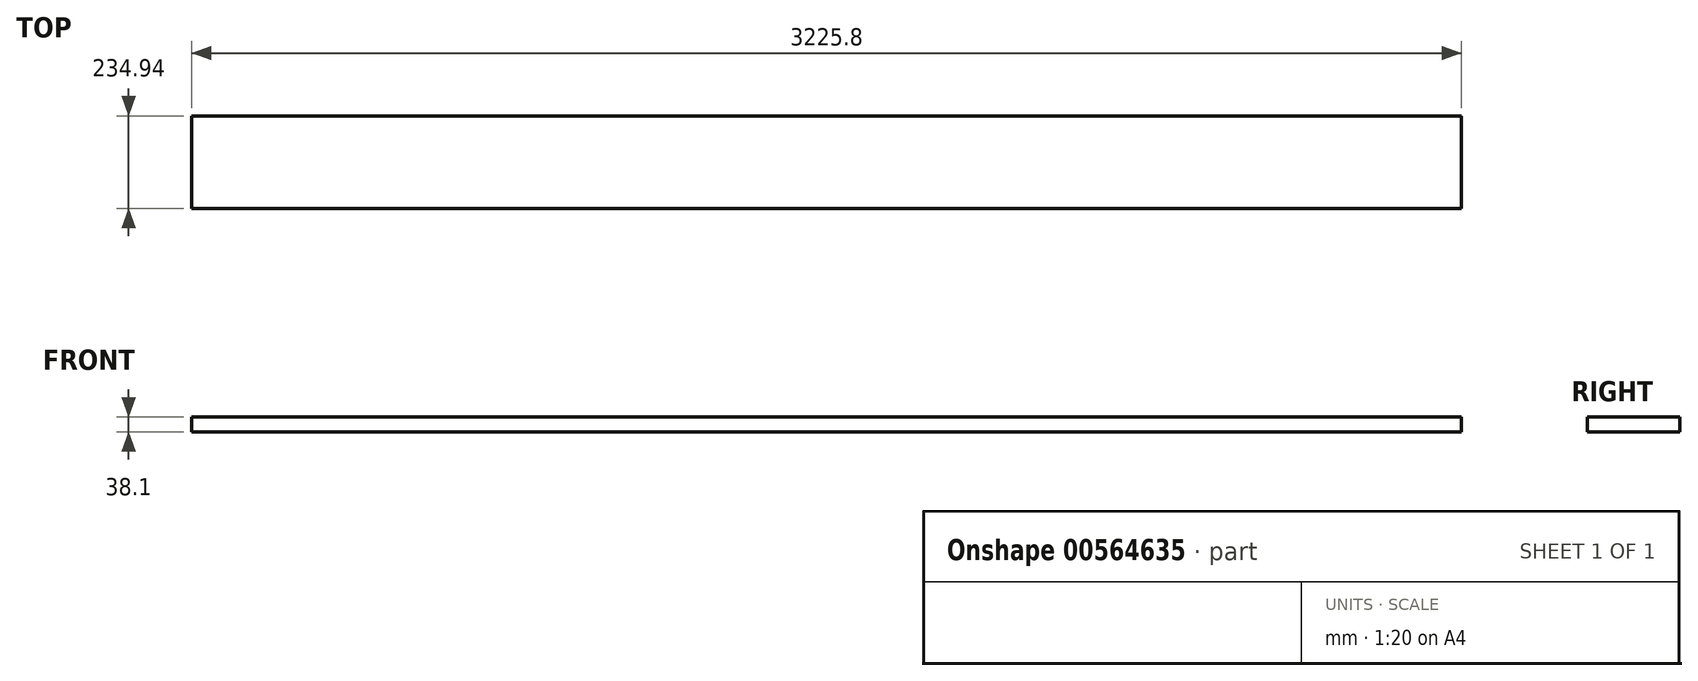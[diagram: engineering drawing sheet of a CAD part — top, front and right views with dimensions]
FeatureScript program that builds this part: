
annotation { "Feature Type Name" : "Feature", "Feature Type Description" : "" }
export const myFeature = defineFeature(function(context is Context, id is Id, definition is map)
    precondition{}
    {
        {
            var Q0;
            Q0=qCreatedBy(makeId("Top.planeOp"),FACE);
            var sketch = newSketch(context, id + "F0", { "sketchPlane" : qUnion([Q0])});
            skLineSegment(sketch, "E0.bottom", {"start": v(-1612.9, 117.48) * mm, "end": v(1612.9, 117.48) * mm});
            skLineSegment(sketch, "E0.top", {"start": v(-1612.9, -117.47) * mm, "end": v(1612.9, -117.47) * mm});
            skLineSegment(sketch, "E0.left", {"start": v(-1612.9, 117.48) * mm, "end": v(-1612.9, -117.47) * mm});
            skLineSegment(sketch, "E0.right", {"start": v(1612.9, 117.48) * mm, "end": v(1612.9, -117.47) * mm});
            skPoint(sketch, "E0.middle", {"position": v(0, 0) * mm});
            skSolve(sketch);
        }
        {
            var Q0;
            Q0=makeQuery(id+"F0.imprint","IMPRINT",FACE,{"disambiguationData":[TD([[makeQuery(id+"F0.imprint","IMPRINT",EDGE,{"derivedFrom":sQuery(id+"F0.wireOp",EDGE,"E0.bottom")}),-1.0]])]});
            extrude(context, id + "F1", {"entities" : qUnion([Q0]), "depth" : 38.1 * mm, "offsetDistance" : 25.4 * mm});
        }
    });
